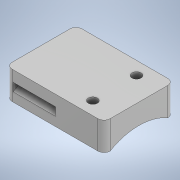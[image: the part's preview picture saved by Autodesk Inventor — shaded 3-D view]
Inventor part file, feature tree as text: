
AUTODESK INVENTOR PART (.ipt)
format: ipt  version: 2021.1 (Build 251245010, 245A)  size: 298,496 bytes
history: native  units: mm
features: move_body x12, other x3, direct_edit x2, fillet x1, extrude x1, sketch x1
ambient origin geometry x8: Origin, YZ Plane, XZ Plane, XY Plane, X Axis, Y Axis, Z Axis, Center Point
bodies: Volumenkörper1 (feature_tree)
feature tree (20):
  direct_edit  "Direktbearbeitung1"
  direct_edit  "Direktbearbeitung2"
  fillet  "Rundung1"  Radius=3.0mm
  extrude  "Extrusion1"  Depth=10.0mm TaperAngle=0.0deg
  sketch  "Skizze1"  dims[d1=3.0mm d2=0.0mm d3=3.0mm d4=0.0mm d5=0.0mm d6=-3.5mm d7=0.0mm d8=0.0mm d9=-0.5mm d10=0.0mm d11=1.75mm d12=0.0mm d13=0.0mm d14=-1.25mm d15=0.0mm d16=0.0mm d17=0.0mm d18=0.0mm d19=-6.75mm d20=0.0mm d21=0.0mm d22=0.5mm d23=0.0mm d24=0.0mm d25=0.5mm d26=0.0mm d27=0.0mm d28=4.5mm d29=0.0mm d30=0.0mm d31=6.5mm d32=2.0mm d33=0.0mm d34=0.0mm d35=1.0mm d36=0.0mm d37=0.0mm d38=1.75mm d39=10.0mm d40=0.0mm]
  other  "Körper1"
  other  "Größe1"
  other  "Größe2"
  move_body  "Verschieben1"
  move_body  "Verschieben2"
  move_body  "Verschieben3"
  move_body  "Verschieben4"
  move_body  "Verschieben5"
  move_body  "Verschieben6"
  move_body  "Verschieben7"
  move_body  "Verschieben8"
  move_body  "Verschieben9"
  move_body  "Verschieben10"
  move_body  "Verschieben11"
  move_body  "Verschieben12"
